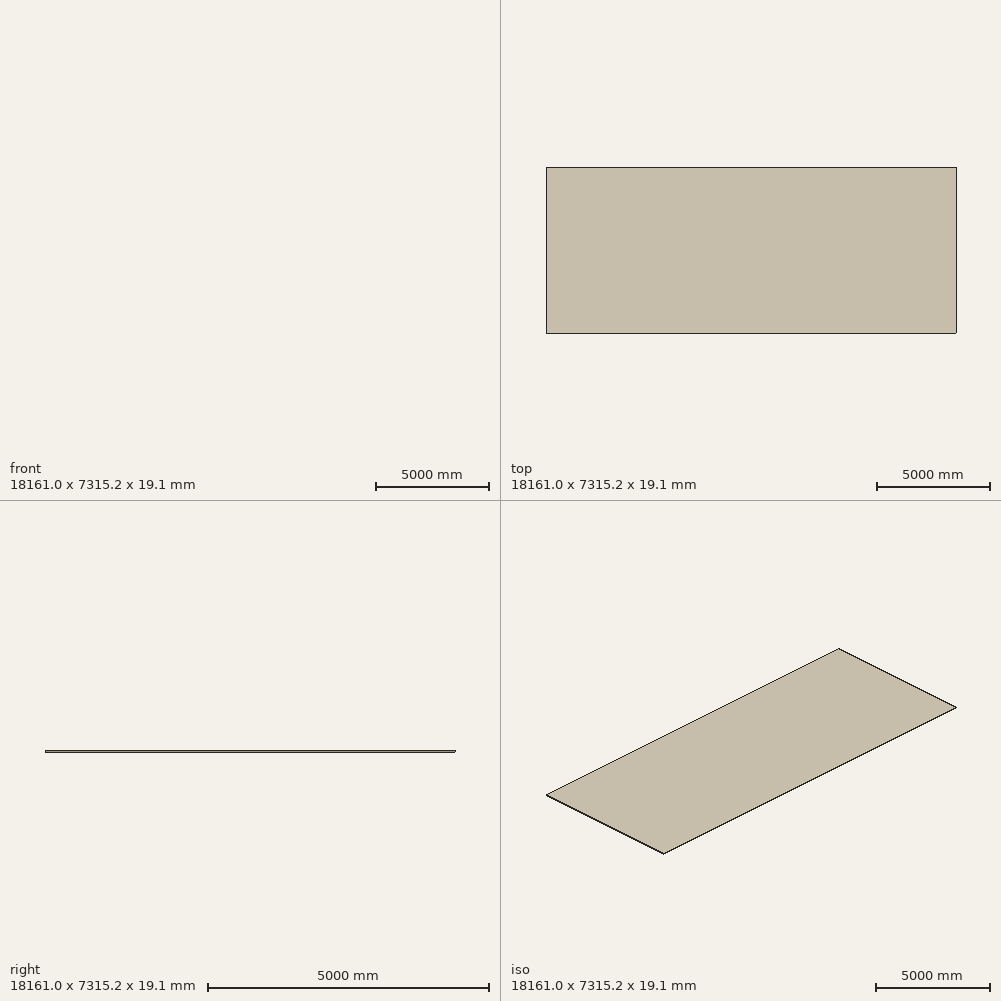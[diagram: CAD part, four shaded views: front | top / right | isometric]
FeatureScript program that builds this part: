
annotation { "Feature Type Name" : "Feature", "Feature Type Description" : "" }
export const myFeature = defineFeature(function(context is Context, id is Id, definition is map)
    precondition{}
    {
        {
            var Q0;
            Q0=qCreatedBy(makeId("Top.planeOp"),FACE);
            var sketch = newSketch(context, id + "F0", { "sketchPlane" : qUnion([Q0])});
            skLineSegment(sketch, "E0.bottom", {"start": v(0, 0) * mm, "end": v(18161, 0) * mm});
            skLineSegment(sketch, "E0.top", {"start": v(0, 7315.2) * mm, "end": v(18161, 7315.2) * mm});
            skLineSegment(sketch, "E0.left", {"start": v(0, 0) * mm, "end": v(0, 7315.2) * mm});
            skLineSegment(sketch, "E0.right", {"start": v(18161, 0) * mm, "end": v(18161, 7315.2) * mm});
            skSolve(sketch);
        }
        {
            var Q0;
            Q0 = qSketchRegion(id + "F0", true);
            extrude(context, id + "F1", {"entities" : qUnion([Q0]), "depth" : 19.05 * mm, "offsetDistance" : 25.4 * mm});
        }
    });
